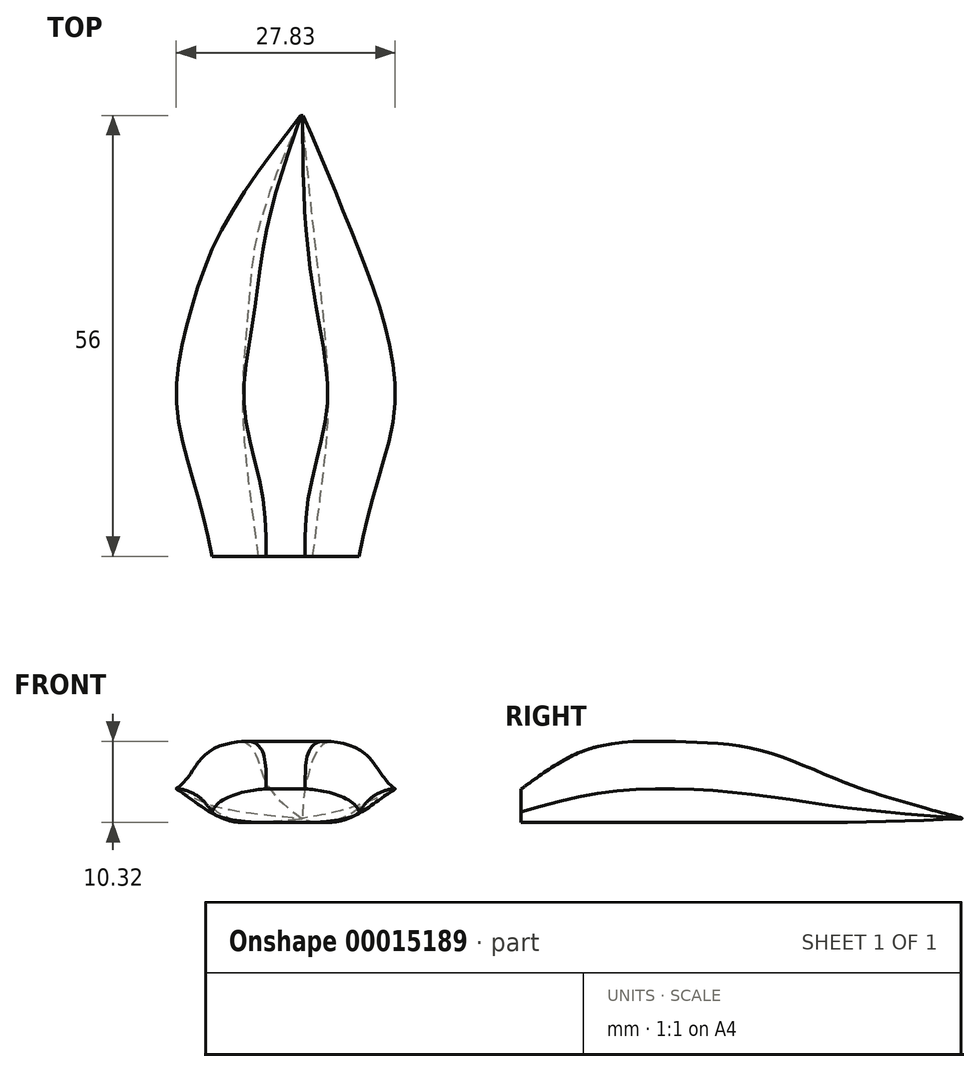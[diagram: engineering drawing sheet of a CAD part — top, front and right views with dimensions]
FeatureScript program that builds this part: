
annotation { "Feature Type Name" : "Feature", "Feature Type Description" : "" }
export const myFeature = defineFeature(function(context is Context, id is Id, definition is map)
    precondition{}
    {
        {
            var Q0;
            Q0=qCreatedBy(makeId("Front.planeOp"),FACE);
            cPlane(context, id + "F0", {"entities" : qUnion([Q0]), "cplaneType" : CPlaneType.OFFSET, "offset" : 25 * mm, "width" : 150 * mm, "height" : 150 * mm});
        }
        {
            var Q0;
            Q0=qCreatedBy(id+"F0.planeOp",FACE);
            cPlane(context, id + "F1", {"entities" : qUnion([Q0]), "cplaneType" : CPlaneType.OFFSET, "offset" : 7 * mm, "oppositeDirection" : true, "width" : 150 * mm, "height" : 150 * mm});
        }
        {
            var Q0;
            Q0=qCreatedBy(id+"F1.planeOp",FACE);
            cPlane(context, id + "F2", {"entities" : qUnion([Q0]), "cplaneType" : CPlaneType.OFFSET, "offset" : 12 * mm, "oppositeDirection" : true, "width" : 150 * mm, "height" : 150 * mm});
        }
        {
            var Q0;
            Q0=qCreatedBy(id+"F2.planeOp",FACE);
            cPlane(context, id + "F3", {"entities" : qUnion([Q0]), "cplaneType" : CPlaneType.OFFSET, "offset" : 12 * mm, "oppositeDirection" : true, "width" : 150 * mm, "height" : 150 * mm});
        }
        {
            var Q0;
            Q0=qCreatedBy(id+"F3.planeOp",FACE);
            cPlane(context, id + "F4", {"entities" : qUnion([Q0]), "cplaneType" : CPlaneType.OFFSET, "offset" : 9 * mm, "oppositeDirection" : true, "width" : 150 * mm, "height" : 150 * mm});
        }
        {
            var Q0;
            Q0=qCreatedBy(id+"F4.planeOp",FACE);
            cPlane(context, id + "F5", {"entities" : qUnion([Q0]), "cplaneType" : CPlaneType.OFFSET, "offset" : 16 * mm, "oppositeDirection" : true, "width" : 150 * mm, "height" : 150 * mm});
        }
        {
            var Q0;
            Q0=qCreatedBy(id+"F0.planeOp",FACE);
            var sketch = newSketch(context, id + "F6", { "sketchPlane" : qUnion([Q0])});
            skLineSegment(sketch, "E0.0", {"start": v(-2.47, 4.25) * mm, "end": v(2.47, 4.25) * mm});
            skLineSegment(sketch, "E0.3", {"start": v(3.44, 0) * mm, "end": v(-3.44, 0) * mm});
            skLineSegment(sketch, "E1", {"start": v(-9.33, 1.34) * mm, "end": v(9.33, 1.34) * mm, "construction": true});
            skLineSegment(sketch, "E2", {"start": v(0, 11.18) * mm, "end": v(0, -13.43) * mm, "construction": true});
            skPoint(sketch, "E2.startSnap0", {"position": v(0, 1.34) * mm});
            skFitSpline(sketch, "E3", {"points": [v(2.47, 4.25) * mm, v(9.33, 1.34) * mm], "startDerivative": vector(6.59, -0.22) * mm, "endDerivative": vector(1.85, -5.94) * mm});
            skFitSpline(sketch, "E4.MirrorCS", {"points": [v(-2.47, 4.25) * mm, v(-9.33, 1.34) * mm], "startDerivative": vector(-6.59, -0.22) * mm, "endDerivative": vector(-1.85, -5.94) * mm});
            skFitSpline(sketch, "E5", {"points": [v(9.33, 1.34) * mm, v(3.44, 0) * mm], "startDerivative": vector(-1.56, -2.83) * mm, "endDerivative": vector(-4.58, 0) * mm});
            skFitSpline(sketch, "E6.MirrorCS", {"points": [v(-9.33, 1.34) * mm, v(-3.44, 0) * mm], "startDerivative": vector(1.56, -2.83) * mm, "endDerivative": vector(4.58, 0) * mm});
            skSolve(sketch);
        }
        {
            var Q0;
            Q0=qCreatedBy(id+"F1.planeOp",FACE);
            var sketch = newSketch(context, id + "F7", { "sketchPlane" : qUnion([Q0])});
            skLineSegment(sketch, "E7.0", {"start": v(-2.82, 8.7) * mm, "end": v(2.82, 8.7) * mm});
            skLineSegment(sketch, "E7.3", {"start": v(4.36, 0) * mm, "end": v(-4.36, 0) * mm});
            skLineSegment(sketch, "E8", {"start": v(-10.96, 3.19) * mm, "end": v(10.96, 3.19) * mm, "construction": true});
            skLineSegment(sketch, "E9", {"start": v(0, 21.79) * mm, "end": v(0, -1.86) * mm, "construction": true});
            skPoint(sketch, "E9.startSnap0", {"position": v(0, 3.19) * mm});
            skPoint(sketch, "E10", {"position": v(0, 9.96) * mm});
            skFitSpline(sketch, "E11", {"points": [v(2.82, 8.7) * mm, v(10.96, 3.19) * mm], "startDerivative": vector(17.04, 0.2) * mm, "endDerivative": vector(3.57, -3.51) * mm});
            skFitSpline(sketch, "E12", {"points": [v(4.36, 0) * mm, v(10.96, 3.19) * mm], "startDerivative": vector(12.37, 0) * mm, "endDerivative": vector(5.04, 3.38) * mm});
            skFitSpline(sketch, "E13.MirrorCS", {"points": [v(-4.36, 0) * mm, v(-10.96, 3.19) * mm], "startDerivative": vector(-12.37, 0) * mm, "endDerivative": vector(-5.04, 3.38) * mm});
            skFitSpline(sketch, "E14.MirrorCS", {"points": [v(-2.82, 8.7) * mm, v(-10.96, 3.19) * mm], "startDerivative": vector(-17.04, 0.2) * mm, "endDerivative": vector(-3.57, -3.51) * mm});
            skSolve(sketch);
        }
        {
            var Q0;
            Q0=qCreatedBy(id+"F2.planeOp",FACE);
            var sketch = newSketch(context, id + "F8", { "sketchPlane" : qUnion([Q0])});
            skLineSegment(sketch, "E15.0", {"start": v(-5.26, 10.27) * mm, "end": v(5.26, 10.27) * mm});
            skLineSegment(sketch, "E15.3", {"start": v(5.42, 0) * mm, "end": v(-5.42, 0) * mm});
            skLineSegment(sketch, "E16", {"start": v(-13.85, 4.29) * mm, "end": v(13.85, 4.29) * mm, "construction": true});
            skLineSegment(sketch, "E17", {"start": v(0, 11.5) * mm, "end": v(0, -12.14) * mm, "construction": true});
            skPoint(sketch, "E17.startSnap0", {"position": v(0, 4.29) * mm});
            skFitSpline(sketch, "E18", {"points": [v(5.26, 10.27) * mm, v(13.85, 4.29) * mm], "startDerivative": vector(19.12, -1.1) * mm, "endDerivative": vector(8.3, -5.83) * mm});
            skFitSpline(sketch, "E19", {"points": [v(13.85, 4.29) * mm, v(5.42, 0) * mm], "startDerivative": vector(-6.85, -4.1) * mm, "endDerivative": vector(-10.75, 0) * mm});
            skFitSpline(sketch, "E20.MirrorCS", {"points": [v(-13.85, 4.29) * mm, v(-5.42, 0) * mm], "startDerivative": vector(6.85, -4.1) * mm, "endDerivative": vector(10.75, 0) * mm});
            skFitSpline(sketch, "E21.MirrorCS", {"points": [v(-5.26, 10.27) * mm, v(-13.85, 4.29) * mm], "startDerivative": vector(-19.12, -1.1) * mm, "endDerivative": vector(-8.3, -5.83) * mm});
            skSolve(sketch);
        }
        {
            var Q0;
            Q0=qCreatedBy(id+"F3.planeOp",FACE);
            var sketch = newSketch(context, id + "F9", { "sketchPlane" : qUnion([Q0])});
            skLineSegment(sketch, "E22.0", {"start": v(-3.97, 9.02) * mm, "end": v(3.97, 9.02) * mm});
            skLineSegment(sketch, "E22.3", {"start": v(4.75, 0) * mm, "end": v(-4.75, 0) * mm});
            skLineSegment(sketch, "E23", {"start": v(-12.11, 3.34) * mm, "end": v(12.11, 3.34) * mm, "construction": true});
            skLineSegment(sketch, "E24", {"start": v(0, 40.4) * mm, "end": v(0, 16.75) * mm, "construction": true});
            skPoint(sketch, "E24.startSnap0", {"position": v(0, 3.34) * mm});
            skFitSpline(sketch, "E25", {"points": [v(3.97, 9.02) * mm, v(12.11, 3.34) * mm], "startDerivative": vector(10.47, -0.78) * mm, "endDerivative": vector(7.97, -4.82) * mm});
            skFitSpline(sketch, "E26", {"points": [v(12.11, 3.34) * mm, v(4.75, 0) * mm], "startDerivative": vector(-7.57, -3.99) * mm, "endDerivative": vector(-10.5, 0) * mm});
            skFitSpline(sketch, "E27.MirrorCS", {"points": [v(-12.11, 3.34) * mm, v(-4.75, 0) * mm], "startDerivative": vector(7.57, -3.99) * mm, "endDerivative": vector(10.5, 0) * mm});
            skFitSpline(sketch, "E28.MirrorCS", {"points": [v(-3.97, 9.02) * mm, v(-12.11, 3.34) * mm], "startDerivative": vector(-10.47, -0.78) * mm, "endDerivative": vector(-7.97, -4.82) * mm});
            skSolve(sketch);
        }
        {
            var Q0;
            Q0=qCreatedBy(id+"F4.planeOp",FACE);
            var sketch = newSketch(context, id + "F10", { "sketchPlane" : qUnion([Q0])});
            skLineSegment(sketch, "E29.0", {"start": v(-2.71, 5.5) * mm, "end": v(2.71, 5.5) * mm});
            skLineSegment(sketch, "E29.3", {"start": v(3.74, 0) * mm, "end": v(-3.74, 0) * mm});
            skLineSegment(sketch, "E30", {"start": v(-8.87, 2.04) * mm, "end": v(8.87, 2.04) * mm, "construction": true});
            skLineSegment(sketch, "E31", {"start": v(0, 27.6) * mm, "end": v(0, 3.95) * mm, "construction": true});
            skPoint(sketch, "E31.startSnap0", {"position": v(0, 2.04) * mm});
            skFitSpline(sketch, "E32", {"points": [v(2.71, 5.5) * mm, v(8.87, 2.04) * mm], "startDerivative": vector(9.64, -0.06) * mm, "endDerivative": vector(6.03, -3.46) * mm});
            skFitSpline(sketch, "E33", {"points": [v(8.87, 2.04) * mm, v(3.74, 0) * mm], "startDerivative": vector(-3.84, -2.48) * mm, "endDerivative": vector(-11.89, 0) * mm});
            skFitSpline(sketch, "E34.MirrorCS", {"points": [v(-8.87, 2.04) * mm, v(-3.74, 0) * mm], "startDerivative": vector(3.84, -2.48) * mm, "endDerivative": vector(11.89, 0) * mm});
            skFitSpline(sketch, "E35.MirrorCS", {"points": [v(-2.71, 5.5) * mm, v(-8.87, 2.04) * mm], "startDerivative": vector(-9.64, -0.06) * mm, "endDerivative": vector(-6.03, -3.46) * mm});
            skSolve(sketch);
        }
        {
            var Q0;
            Q0=qCreatedBy(id+"F5.planeOp",FACE);
            var sketch = newSketch(context, id + "F11", { "sketchPlane" : qUnion([Q0])});
            skLineSegment(sketch, "E36.0", {"start": v(1.98, 0.56) * mm, "end": v(2.14, 0.56) * mm});
            skLineSegment(sketch, "E36.3", {"start": v(2.1, 0.47) * mm, "end": v(2.01, 0.47) * mm});
            skLineSegment(sketch, "E37", {"start": v(0.17, 0.52) * mm, "end": v(1.89, 0.52) * mm, "construction": true});
            skLineSegment(sketch, "E38", {"start": v(2.06, 4.63) * mm, "end": v(2.06, -1.74) * mm, "construction": true});
            skPoint(sketch, "E38.startSnap0", {"position": v(1.03, 0.52) * mm});
            skFitSpline(sketch, "E39", {"points": [v(1.98, 0.56) * mm, v(1.89, 0.52) * mm], "startDerivative": vector(-0.17, 0) * mm, "endDerivative": vector(-0.12, -0.08) * mm});
            skFitSpline(sketch, "E40", {"points": [v(1.89, 0.52) * mm, v(2.01, 0.47) * mm], "startDerivative": vector(0.1, -0.1) * mm, "endDerivative": vector(0.27, -0.06) * mm});
            skFitSpline(sketch, "E41.MirrorCS", {"points": [v(2.23, 0.52) * mm, v(2.1, 0.47) * mm], "startDerivative": vector(-0.1, -0.1) * mm, "endDerivative": vector(-0.27, -0.06) * mm});
            skFitSpline(sketch, "E42.MirrorCS", {"points": [v(2.14, 0.56) * mm, v(2.23, 0.52) * mm], "startDerivative": vector(0.17, 0) * mm, "endDerivative": vector(0.12, -0.08) * mm});
            skSolve(sketch);
        }
        {
            var Q0;
            Q0 = qSketchRegion(id + "F6", true);
            var Q1;
            Q1 = qSketchRegion(id + "F7", true);
            var Q2;
            Q2 = qSketchRegion(id + "F8", true);
            var Q3;
            Q3 = qSketchRegion(id + "F9", true);
            var Q4;
            Q4 = qSketchRegion(id + "F10", true);
            var Q5;
            Q5 = qSketchRegion(id + "F11", true);
            loft(context, id + "F12", {"sheetProfilesArray" : [{ "sheetProfileEntities" : qUnion([Q0]) }, { "sheetProfileEntities" : qUnion([Q1]) }, { "sheetProfileEntities" : qUnion([Q2]) }, { "sheetProfileEntities" : qUnion([Q3]) }, { "sheetProfileEntities" : qUnion([Q4]) }, { "sheetProfileEntities" : qUnion([Q5]) }]});
        }
    });
